# Revit family: Gira_015000
name_source: partatom
category: Allgemeines Modell
revit_build: Autodesk Revit 2017 (Build: 20160225_1515(x64)
units: mm (PartAtom-declared; Revit-internal decimal feet)

## family parameters
Basisbauteil = Fläche
Beim Laden mit Abzugskörper schneiden = Nein
Bemaßung runder Anschluss = Durchmesser verwenden
Gemeinsam genutzt = Nein
Kann Basisbauteil für Bewehrung sein = Nein
Raumberechnungspunkt = Nein
Teiletyp = Normal

## types (1)
- Gira_015000
    Andere Bussysteme = ohne
    Anschlussart = Schraubklemme
    Anzahl der Betätigungswippen = 1
    App-Steuerung über Bluetooth = Nein
    Aufdruck = ohne
    Ausführung = Einzeltaster
    Ausführung der Oberfläche = nicht zutreffend
    Aussperrsicherung = Nein
    BIM = https://media.stage.bim.site
    Bedienungsart = Wippe
    Befestigungsart = Krallen-/Schraubbefestigung
    Bemessungsstrom = 10 A
    Beschreibung = Einsatz Wipptaster 10 AX 250 V~  Schließer 1-polig mit N-Klemme Hinweise : - Auch beleuchtet anschließbar.
    Bussystem Funkbus = Nein
    Bussystem KNX = Ja
    Bussystem KNX-Funk = Nein
    Bussystem LON = Nein
    Bussystem Powernet = Nein
    Datenblatt = https://katalog.gira.de
    Dimmung Phasenabschnitt = Nein
    Dimmung Phasenanschnitt = Nein
    Farbe = sonstige
    Frequenz [Hz] = [50:50]
    Funk bidirektional = Nein
    GTIN = 4010337150008
    Geeignet für Regensensor = Nein
    Geeignet für Schutzart (IP) = IP20
    Geeignet für Windsensor = Nein
    HAN = 015000
    Halogenfrei = Nein
    Hersteller = Gira
    Integrierte Zeitschaltuhr = Nein
    Kontakte = 1 Schließer
    Lastart = sonstige
    Lichtwertspeicher = Nein
    Max. Schaltleistung [Voltampere] = 1000
    Mit Astro-Programm = Nein
    Mit Beleuchtung = Nein
    Mit Glasbruchmelderanschluss = Nein
    Mit Helligkeitssensoranschluss = Nein
    Mit Memory-Funktion = Nein
    Montageart = Unterputz
    Nebenstelleneingang = Ja
    Nennspannung [Volt] = [230:230]
    Nennspannung [Volt] 1 = 230
    Nennspannung [Volt] 13 = 250
    Nennspannung [Volt] 17 = 250
    Nennspannung [Volt] 2 = 230
    Nennspannung [Volt] 5 = 230
    Oberfläche = sonstige
    Produktseite = http://katalog.gira.de
    Rückmeldekontakt = Nein
    Seriendimmer = Nein
    Textfeld/Beschriftungsfläche = Nein
    Transparent = Nein
    Typname = Wipptaster Schließer + N-Kl. Einsatz
    URL = https://www.gira.de
    Verwendbar mit Bewegungsmelder = Nein
    Verwendbar mit Funktaste = Nein
    Verwendbar mit IR-Taste = Nein
    Verwendbar mit Präsenzmelder = Nein
    Verwendbar mit Taste = Ja
    Verwendbar mit Zeitschalter/Timer = Nein
    Vorgabe-Ansicht = 1219 mm
    Werkstoff = sonstige
    Werkstoffgüte = sonstige
    Zufallsgenerator = Nein
    Zusammenstellung = Basiselement

## geometry (parser evidence)
native form markers: Sweep x2
no freeform markers — native parametric forms only
